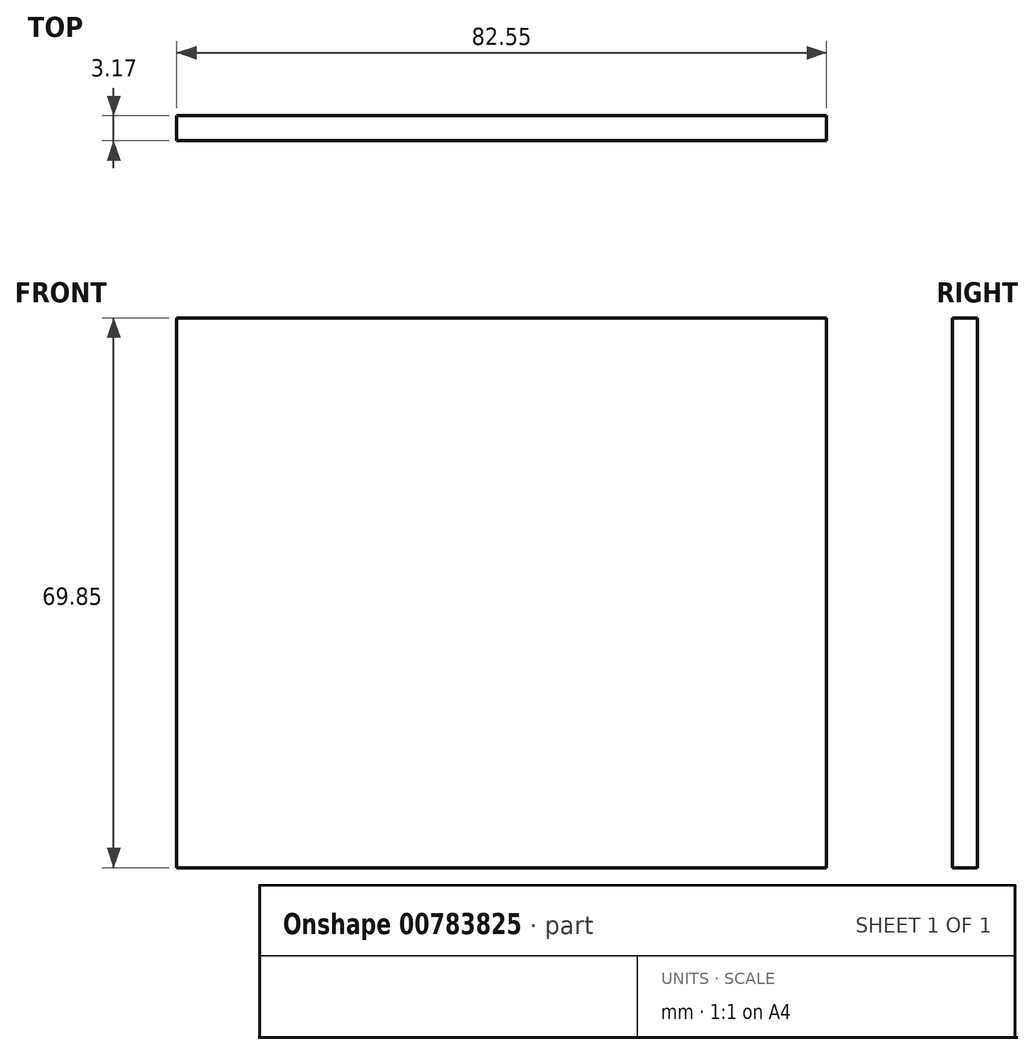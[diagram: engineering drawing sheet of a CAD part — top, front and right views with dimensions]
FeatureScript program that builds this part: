
annotation { "Feature Type Name" : "Feature", "Feature Type Description" : "" }
export const myFeature = defineFeature(function(context is Context, id is Id, definition is map)
    precondition{}
    {
        {
            var Q0;
            Q0=qCreatedBy(makeId("Front.planeOp"),FACE);
            var sketch = newSketch(context, id + "F0", { "sketchPlane" : qUnion([Q0])});
            skLineSegment(sketch, "E0.bottom", {"start": v(-67.22, 50.12) * mm, "end": v(15.33, 50.12) * mm});
            skLineSegment(sketch, "E0.top", {"start": v(-67.22, -19.73) * mm, "end": v(15.33, -19.73) * mm});
            skLineSegment(sketch, "E0.left", {"start": v(-67.22, 50.12) * mm, "end": v(-67.22, -19.73) * mm});
            skLineSegment(sketch, "E0.right", {"start": v(15.33, 50.12) * mm, "end": v(15.33, -19.73) * mm});
            skSolve(sketch);
        }
        {
            var Q0;
            Q0=makeQuery(id+"F0.imprint","IMPRINT",FACE,{"disambiguationData":[TD([[makeQuery(id+"F0.imprint","IMPRINT",EDGE,{"derivedFrom":sQuery(id+"F0.wireOp",EDGE,"E0.bottom")}),-1.0]])]});
            extrude(context, id + "F1", {"entities" : qUnion([Q0]), "depth" : 3.17 * mm, "offsetDistance" : 25.4 * mm});
        }
    });
